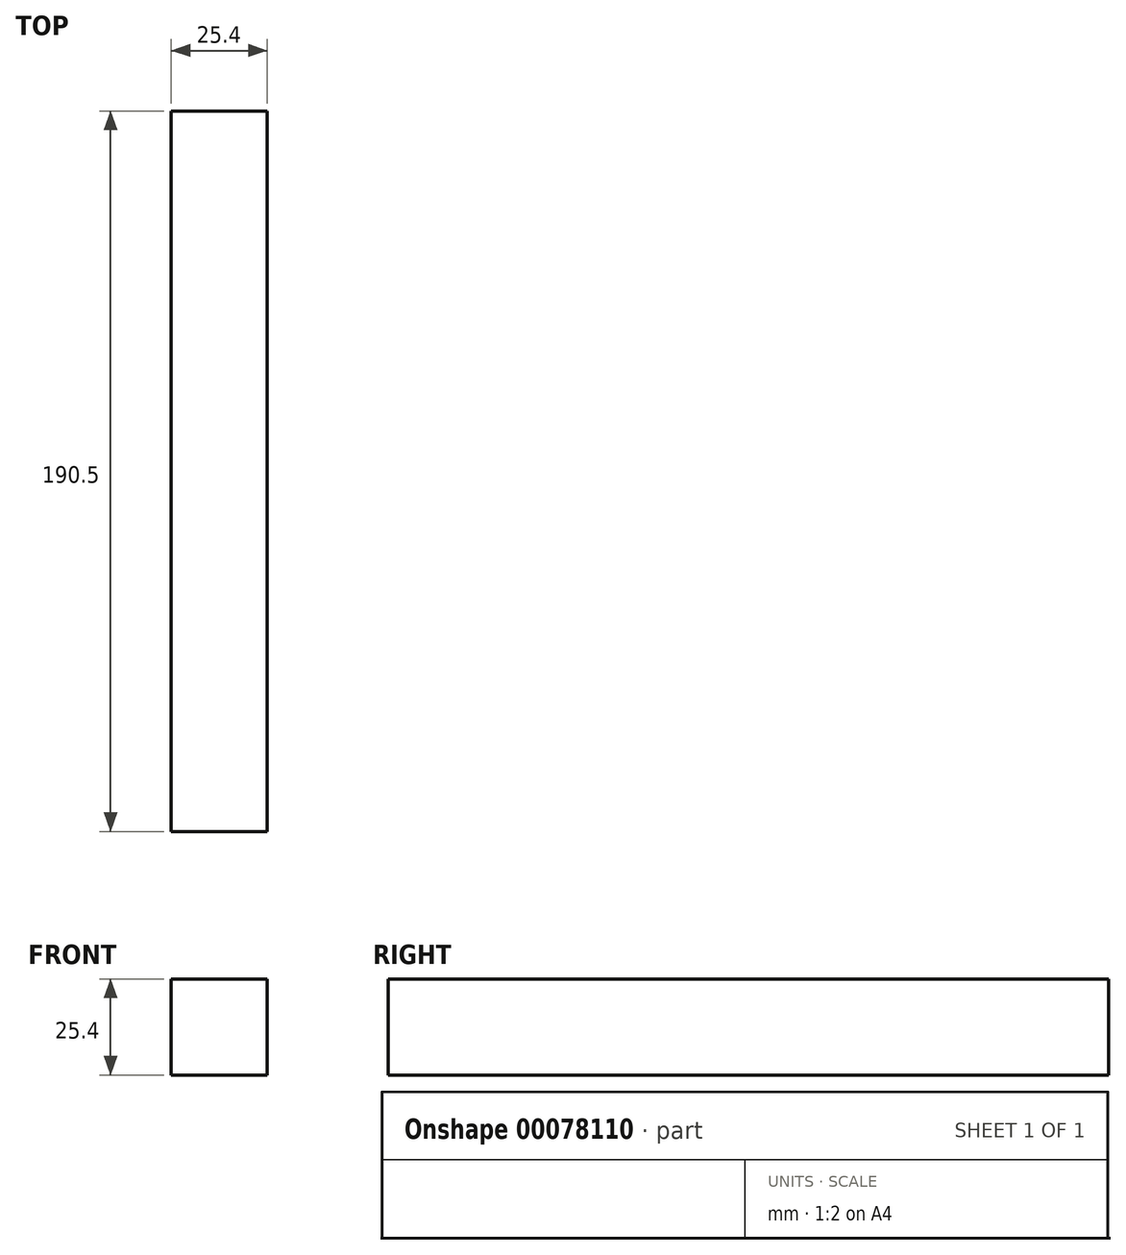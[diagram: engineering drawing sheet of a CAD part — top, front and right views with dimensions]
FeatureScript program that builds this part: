
annotation { "Feature Type Name" : "Feature", "Feature Type Description" : "" }
export const myFeature = defineFeature(function(context is Context, id is Id, definition is map)
    precondition{}
    {
        {
            var Q0;
            Q0=qCreatedBy(makeId("Front.planeOp"),FACE);
            var sketch = newSketch(context, id + "F0", { "sketchPlane" : qUnion([Q0])});
            skLineSegment(sketch, "E0.bottom", {"start": v(0, 0) * mm, "end": v(-25.4, 0) * mm});
            skLineSegment(sketch, "E0.top", {"start": v(0, 25.4) * mm, "end": v(-25.4, 25.4) * mm});
            skLineSegment(sketch, "E0.left", {"start": v(0, 0) * mm, "end": v(0, 25.4) * mm});
            skLineSegment(sketch, "E0.right", {"start": v(-25.4, 0) * mm, "end": v(-25.4, 25.4) * mm});
            skSolve(sketch);
        }
        {
            var Q0;
            Q0=makeQuery(id+"F0.imprint","IMPRINT",FACE,{"disambiguationData":[TD([[makeQuery(id+"F0.imprint","IMPRINT",EDGE,{"derivedFrom":sQuery(id+"F0.wireOp",EDGE,"E0.bottom")}),-1.0]])]});
            extrude(context, id + "F1", {"entities" : qUnion([Q0]), "depth" : 190.5 * mm});
        }
    });
